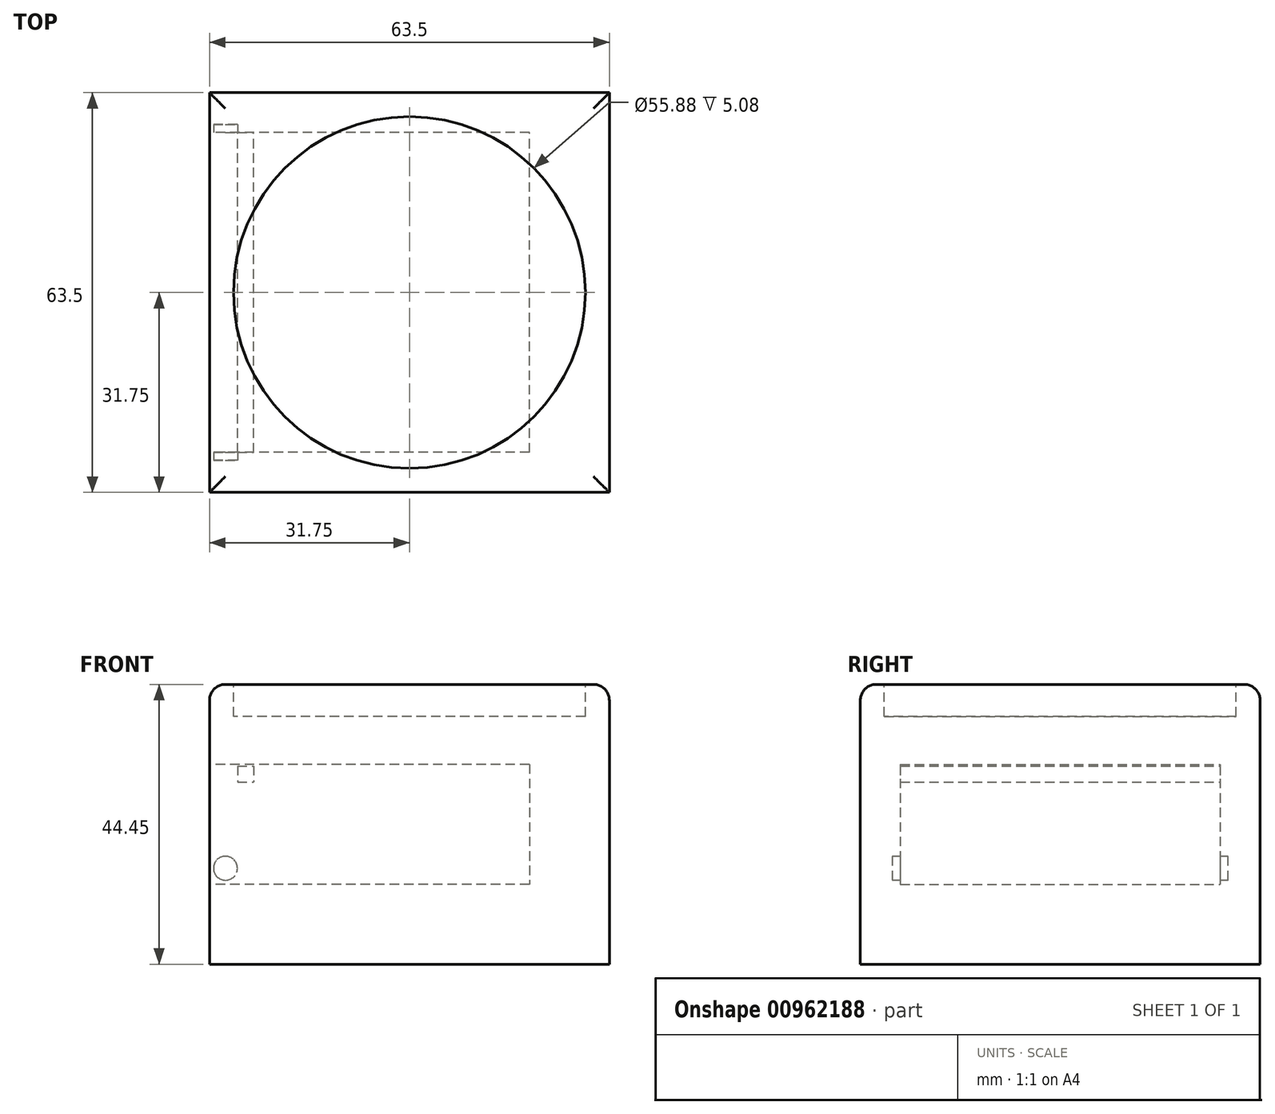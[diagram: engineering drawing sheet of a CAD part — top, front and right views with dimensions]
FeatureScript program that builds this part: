
annotation { "Feature Type Name" : "Feature", "Feature Type Description" : "" }
export const myFeature = defineFeature(function(context is Context, id is Id, definition is map)
    precondition{}
    {
        {
            var Q0;
            Q0=qCreatedBy(makeId("Top.planeOp"),FACE);
            var sketch = newSketch(context, id + "F0", { "sketchPlane" : qUnion([Q0])});
            skLineSegment(sketch, "E0.bottom", {"start": v(31.75, 31.75) * mm, "end": v(-31.75, 31.75) * mm});
            skLineSegment(sketch, "E0.top", {"start": v(31.75, -31.75) * mm, "end": v(-31.75, -31.75) * mm});
            skLineSegment(sketch, "E0.left", {"start": v(31.75, 31.75) * mm, "end": v(31.75, -31.75) * mm});
            skLineSegment(sketch, "E0.right", {"start": v(-31.75, 31.75) * mm, "end": v(-31.75, -31.75) * mm});
            skPoint(sketch, "E0.middle", {"position": v(0, 0) * mm});
            skSolve(sketch);
        }
        {
            var Q0;
            Q0=makeQuery(id+"F0.imprint","IMPRINT",FACE,{"disambiguationData":[TD([[makeQuery(id+"F0.imprint","IMPRINT",EDGE,{"derivedFrom":sQuery(id+"F0.wireOp",EDGE,"E0.bottom")}),1.0]])]});
            extrude(context, id + "F1", {"entities" : qUnion([Q0]), "depth" : 44.45 * mm, "offsetDistance" : 25.4 * mm});
        }
        {
            var Q0;
            Q0=makeQuery(id+"F1.opExtrude","CAP_FACE",FACE,{"disambiguationData":[OSD([sQuery(id+"F0.wireOp",EDGE,"E0.bottom"),sQuery(id+"F0.wireOp",EDGE,"E0.top"),sQuery(id+"F0.wireOp",EDGE,"E0.left"),sQuery(id+"F0.wireOp",EDGE,"E0.right")])],"isStart":false});
            var sketch = newSketch(context, id + "F2", { "sketchPlane" : qUnion([Q0])});
            skCircle(sketch, "E1", {"center": v(0, 0) * mm, "radius": 27.94 * mm});
            skSolve(sketch);
        }
        {
            var Q0;
            Q0=makeQuery(id+"F2.imprint","IMPRINT",FACE,{"disambiguationData":[TD([[makeQuery(id+"F2.imprint","IMPRINT",EDGE,{"derivedFrom":sQuery(id+"F2.wireOp",EDGE,"E1")}),1.0]])]});
            extrude(context, id + "F3", {"entities" : qUnion([Q0]), "operationType" : NewBodyOperationType.REMOVE, "oppositeDirection" : true, "depth" : 5.08 * mm, "offsetDistance" : 25.4 * mm});
        }
        {
            var Q0;
            Q0=makeQuery(id+"F1.opExtrude","SWEPT_FACE",FACE,{"disambiguationData":[OSD([sQuery(id+"F0.wireOp",EDGE,"E0.right")])]});
            var sketch = newSketch(context, id + "F4", { "sketchPlane" : qUnion([Q0])});
            skLineSegment(sketch, "E2.bottom", {"start": v(25.4, 31.75) * mm, "end": v(-25.4, 31.75) * mm});
            skLineSegment(sketch, "E2.top", {"start": v(25.4, 12.7) * mm, "end": v(-25.4, 12.7) * mm});
            skLineSegment(sketch, "E2.left", {"start": v(25.4, 31.75) * mm, "end": v(25.4, 12.7) * mm});
            skLineSegment(sketch, "E2.right", {"start": v(-25.4, 31.75) * mm, "end": v(-25.4, 12.7) * mm});
            skPoint(sketch, "E2.middle", {"position": v(0, 22.23) * mm});
            skPoint(sketch, "E2.middle.positionSnap0", {"position": v(-31.75, 22.23) * mm});
            skPoint(sketch, "E2.centerSnap0", {"position": v(-31.75, 22.23) * mm});
            skSolve(sketch);
        }
        {
            var Q0;
            Q0=makeQuery(id+"F4.imprint","IMPRINT",FACE,{"disambiguationData":[TD([[makeQuery(id+"F4.imprint","IMPRINT",EDGE,{"derivedFrom":sQuery(id+"F4.wireOp",EDGE,"E2.bottom")}),1.0]])]});
            extrude(context, id + "F5", {"entities" : qUnion([Q0]), "operationType" : NewBodyOperationType.REMOVE, "oppositeDirection" : true, "depth" : 50.8 * mm, "offsetDistance" : 25.4 * mm});
        }
        {
            var Q0;
            Q0=makeQuery(id+"F5.boolean.opBoolean","COPY",FACE,{"derivedFrom":makeQuery(id+"F5.opExtrude","SWEPT_FACE",FACE,{"disambiguationData":[OSD([sQuery(id+"F4.wireOp",EDGE,"E2.right")])]})});
            var sketch = newSketch(context, id + "F6", { "sketchPlane" : qUnion([Q0])});
            skCircle(sketch, "E3", {"center": v(-29.21, 15.24) * mm, "radius": 1.9 * mm});
            skSolve(sketch);
        }
        {
            var Q0;
            Q0=makeQuery(id+"F5.boolean.opBoolean","COPY",FACE,{"derivedFrom":makeQuery(id+"F5.opExtrude","SWEPT_FACE",FACE,{"disambiguationData":[OSD([sQuery(id+"F4.wireOp",EDGE,"E2.left")])]})});
            var sketch = newSketch(context, id + "F7", { "sketchPlane" : qUnion([Q0])});
            skCircle(sketch, "E4", {"center": v(29.21, 15.24) * mm, "radius": 1.9 * mm});
            skSolve(sketch);
        }
        {
            var Q0;
            Q0=makeQuery(id+"F7.imprint","IMPRINT",FACE,{"disambiguationData":[TD([[makeQuery(id+"F7.imprint","IMPRINT",EDGE,{"derivedFrom":sQuery(id+"F7.wireOp",EDGE,"E4")}),1.0]])]});
            var Q1;
            Q1=makeQuery(id+"F6.imprint","IMPRINT",FACE,{"disambiguationData":[TD([[makeQuery(id+"F6.imprint","IMPRINT",EDGE,{"derivedFrom":sQuery(id+"F6.wireOp",EDGE,"E3")}),1.0]])]});
            extrude(context, id + "F8", {"entities" : qUnion([Q0, Q1]), "operationType" : NewBodyOperationType.REMOVE, "endBound" : BoundingType.SYMMETRIC, "depth" : 2.54 * mm, "offsetDistance" : 25.4 * mm});
        }
        {
            var Q0;
            Q0=makeQuery(id+"F1.opExtrude","CAP_EDGE",EDGE,{"disambiguationData":[OSD([sQuery(id+"F0.wireOp",EDGE,"E0.bottom")])],"isStart":false});
            var Q1;
            Q1=makeQuery(id+"F1.opExtrude","CAP_EDGE",EDGE,{"disambiguationData":[OSD([sQuery(id+"F0.wireOp",EDGE,"E0.right")])],"isStart":false});
            var Q2;
            Q2=makeQuery(id+"F1.opExtrude","CAP_EDGE",EDGE,{"disambiguationData":[OSD([sQuery(id+"F0.wireOp",EDGE,"E0.left")])],"isStart":false});
            var Q3;
            Q3=makeQuery(id+"F1.opExtrude","CAP_EDGE",EDGE,{"disambiguationData":[OSD([sQuery(id+"F0.wireOp",EDGE,"E0.top")])],"isStart":false});
            fillet(context, id + "F9", {"entities" : qUnion([Q0, Q1, Q2, Q3]), "radius" : 2.54 * mm, "tangentPropagation" : true, "allowEdgeOverflow" : false});
        }
        {
            var Q0;
            Q0=makeQuery(id+"F5.boolean.opBoolean","COPY",FACE,{"derivedFrom":makeQuery(id+"F5.opExtrude","SWEPT_FACE",FACE,{"disambiguationData":[OSD([sQuery(id+"F4.wireOp",EDGE,"E2.right")])]})});
            var sketch = newSketch(context, id + "F10", { "sketchPlane" : qUnion([Q0])});
            skLineSegment(sketch, "E5.bottom", {"start": v(-27.3, 31.5) * mm, "end": v(-24.77, 31.5) * mm});
            skLineSegment(sketch, "E5.top", {"start": v(-27.3, 28.96) * mm, "end": v(-24.77, 28.96) * mm});
            skLineSegment(sketch, "E5.left", {"start": v(-27.3, 31.5) * mm, "end": v(-27.3, 28.96) * mm});
            skLineSegment(sketch, "E5.right", {"start": v(-24.77, 31.5) * mm, "end": v(-24.77, 28.96) * mm});
            skSolve(sketch);
        }
        {
            var Q0;
            Q0=makeQuery(id+"F10.imprint","IMPRINT",FACE,{"disambiguationData":[TD([[makeQuery(id+"F10.imprint","IMPRINT",EDGE,{"derivedFrom":sQuery(id+"F10.wireOp",EDGE,"E5.bottom")}),-1.0]])]});
            extrude(context, id + "F11", {"entities" : qUnion([Q0]), "operationType" : NewBodyOperationType.ADD, "depth" : 50.8 * mm, "offsetDistance" : 25.4 * mm});
        }
    });
